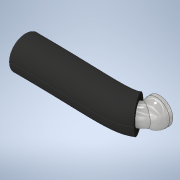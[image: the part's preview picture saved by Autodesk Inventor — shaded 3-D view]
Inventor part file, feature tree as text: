
AUTODESK INVENTOR PART (.ipt)
format: ipt  version: 2020.1 (Build 241239000, 239)  size: 243,200 bytes
history: native  units: mm
features: sketch x6, sweep x2, extrude x1, fillet x1, plane x1
ambient origin geometry x8: Origin, YZ Plane, XZ Plane, XY Plane, X Axis, Y Axis, Z Axis, Center Point
bodies: Solid1 (feature_tree)
feature tree (11):
  extrude  "Extrusion1"  Depth=2.5mm TaperAngle=0.0deg
  fillet  "Fillet1"  Radius=2.0mm
  sweep  "Sweep1"
  plane  "Work Plane1"
  sweep  "Sweep4"
  sketch  "Sketch6"  dims[d19=-2.0mm d20=0.0mm d21=0.0mm]
  sketch  "Sketch1"  dims[d0=4.0mm d1=2.5mm d2=0.0mm d3=2.0mm]
  sketch  "Sketch2"  dims[d4=2.6mm d5=3.06mm]
  sketch  "Sketch3"  dims[d6=0.0mm d7=0.0mm d9=5.0mm]
  sketch  "Sketch4"  dims[d18=4.0mm]
  sketch  "3D Sketch1"
